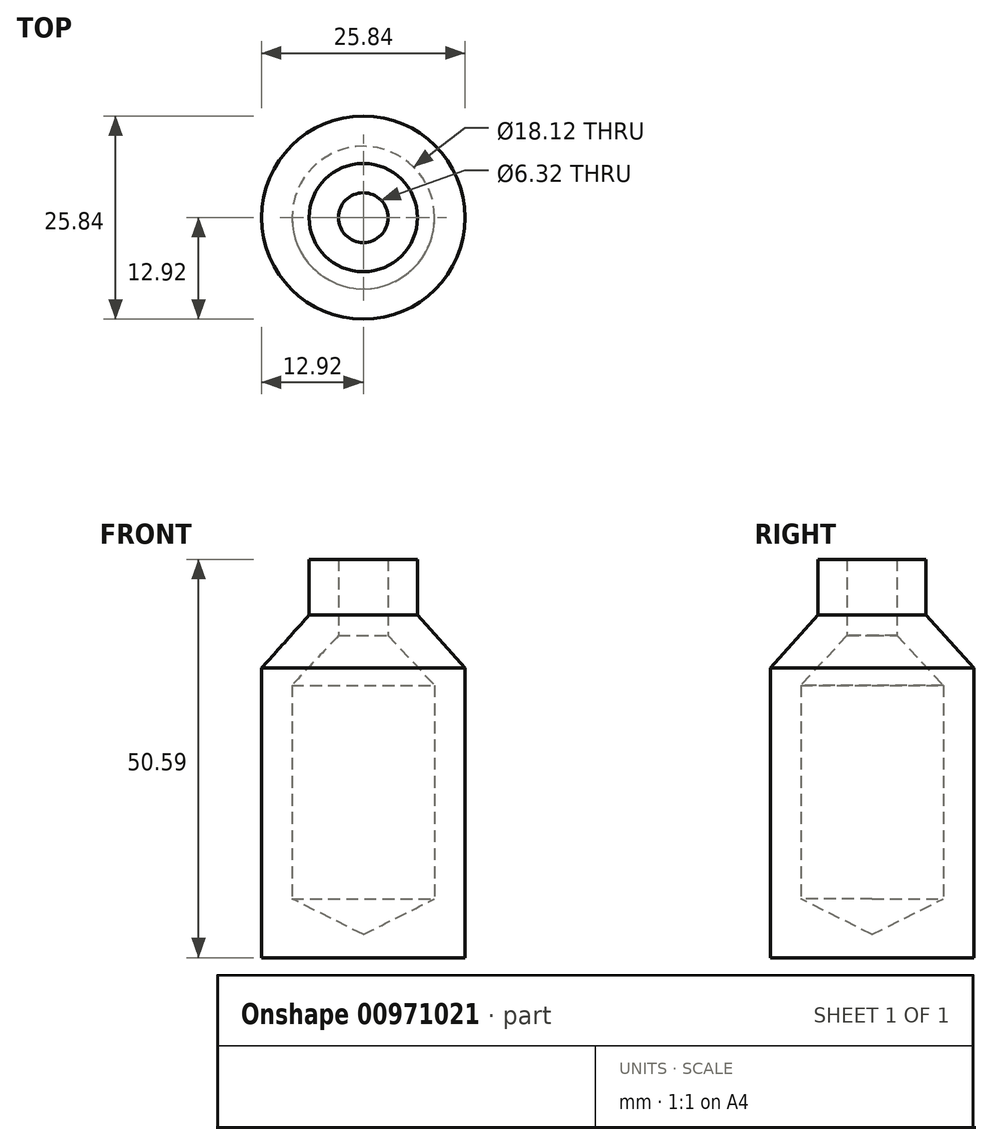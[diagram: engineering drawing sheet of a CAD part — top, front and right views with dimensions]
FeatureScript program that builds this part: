
annotation { "Feature Type Name" : "Feature", "Feature Type Description" : "" }
export const myFeature = defineFeature(function(context is Context, id is Id, definition is map)
    precondition{}
    {
        {
            var Q0;
            Q0=qCreatedBy(makeId("Front.planeOp"),FACE);
            var sketch = newSketch(context, id + "F0", { "sketchPlane" : qUnion([Q0])});
            skLineSegment(sketch, "E0", {"start": v(3.16, 0) * mm, "end": v(6.88, 0) * mm});
            skLineSegment(sketch, "E1", {"start": v(6.88, 0) * mm, "end": v(6.88, -7.07) * mm});
            skLineSegment(sketch, "E2", {"start": v(6.88, -7.07) * mm, "end": v(12.92, -13.8) * mm});
            skLineSegment(sketch, "E3", {"start": v(12.92, -13.8) * mm, "end": v(12.92, -50.6) * mm});
            skLineSegment(sketch, "E4", {"start": v(12.92, -50.6) * mm, "end": v(3.16, -50.6) * mm});
            skLineSegment(sketch, "E5", {"start": v(3.16, -50.6) * mm, "end": v(0, -50.6) * mm});
            skLineSegment(sketch, "E6", {"start": v(0, -50.6) * mm, "end": v(0, -47.64) * mm});
            skLineSegment(sketch, "E7", {"start": v(9.06, -43.13) * mm, "end": v(9.06, -16) * mm});
            skLineSegment(sketch, "E8", {"start": v(9.06, -16) * mm, "end": v(3.16, -9.68) * mm});
            skLineSegment(sketch, "E9", {"start": v(3.16, -9.68) * mm, "end": v(3.16, 0) * mm});
            skLineSegment(sketch, "E10", {"start": v(0, -47.64) * mm, "end": v(9.06, -43.13) * mm});
            skSolve(sketch);
        }
        {
            var Q0;
            Q0=makeQuery(id+"F0.imprint","IMPRINT",FACE,{"disambiguationData":[TD([[makeQuery(id+"F0.imprint","IMPRINT",EDGE,{"derivedFrom":sQuery(id+"F0.wireOp",EDGE,"E0")}),-1.0]])]});
            var Q1;
            Q1=sQuery(id+"F0.wireOp",EDGE,"E6");
            revolve(context, id + "F1", {"surfaceOperationType" : NewSurfaceOperationType.NEW, "entities" : qUnion([Q0]), "axis" : qUnion([Q1]), "revolveType" : RevolveType.FULL});
        }
    });
